# Revit family: Toilet-Floor_Mount-KOHLER-Reach_Up-K-23188X
name_source: partatom
category: Plumbing Fixtures
units: mm (PartAtom-declared; Revit-internal decimal feet)

## family parameters
Cut with Voids When Loaded = No
Host = Face
Maintain Annotation Orientation = No
OmniClass Number = 23.31.19.00
Part Type = Normal
Room Calculation Point = No
Round Connector Dimension = Use Diameter
Shared = No

## types (3) — shared parameters
ADA Compliant = No
Apparent Load = 2200 VA
Assembly Code = D2010100
Bowl Height = 15 9/16"
CW Connection = Yes
Cold Water Inlet 1 = Cold Water Inlet 1
Cold Water Inlet 2 = Cold Water Inlet 2
Date Modified = 06/23/2025
Default Elevation = 0"
Electrical Connector = Yes
Electrical Note = One Dedicated circuit Required
Finish = Kohler-Vitreous_China-0-White
Flow Rate = 0 GPM
Flush Rate- GPF = 1.28 GPF
Flush Rate- LPF = 4.8 LPF
HW Connection = No
Height = 29 9/16"
Hot Water Inlet = Hot Water Inlet
Length = 27 9/16"
Manufacturer = Kohler Co.
Master Format 2014 = 22 42 13.13
Master Format 2014 Name = Residential Water Closets
Material = Vitreous China
Pressure = 0.00 psi
Product Name = Reach Up
Rough-In = 12"
Seat Included = No
URL = https://www.kohler.co.th
Vent Connection = No
Voltage = 220 V
Waste Connection = Yes
Waste Water Outlet = Waste Water Outlet
WaterSense Certified = No
Width = 14 7/8"

## per-type parameters (varying)
| type | C | CCT | Description | Model | NS | Type |
| 0-White | No | No | 1 Piece CS-Trap Without Seat | K-23188X-NS-0 | Yes | 1 |
| C, 0-White | Yes | No | Family care skirted 1PC 3/4.8L  W/QC Seat | K-23188X-C-0 | No | 2 |
| CCT, 0-White | No | Yes | Family care 1PC W/QC SEAT CS-TRAP | K-23188X-CCT-0 | No | 3 |

## geometry (parser evidence)
native form markers: Sweep x11
no freeform markers — native parametric forms only
